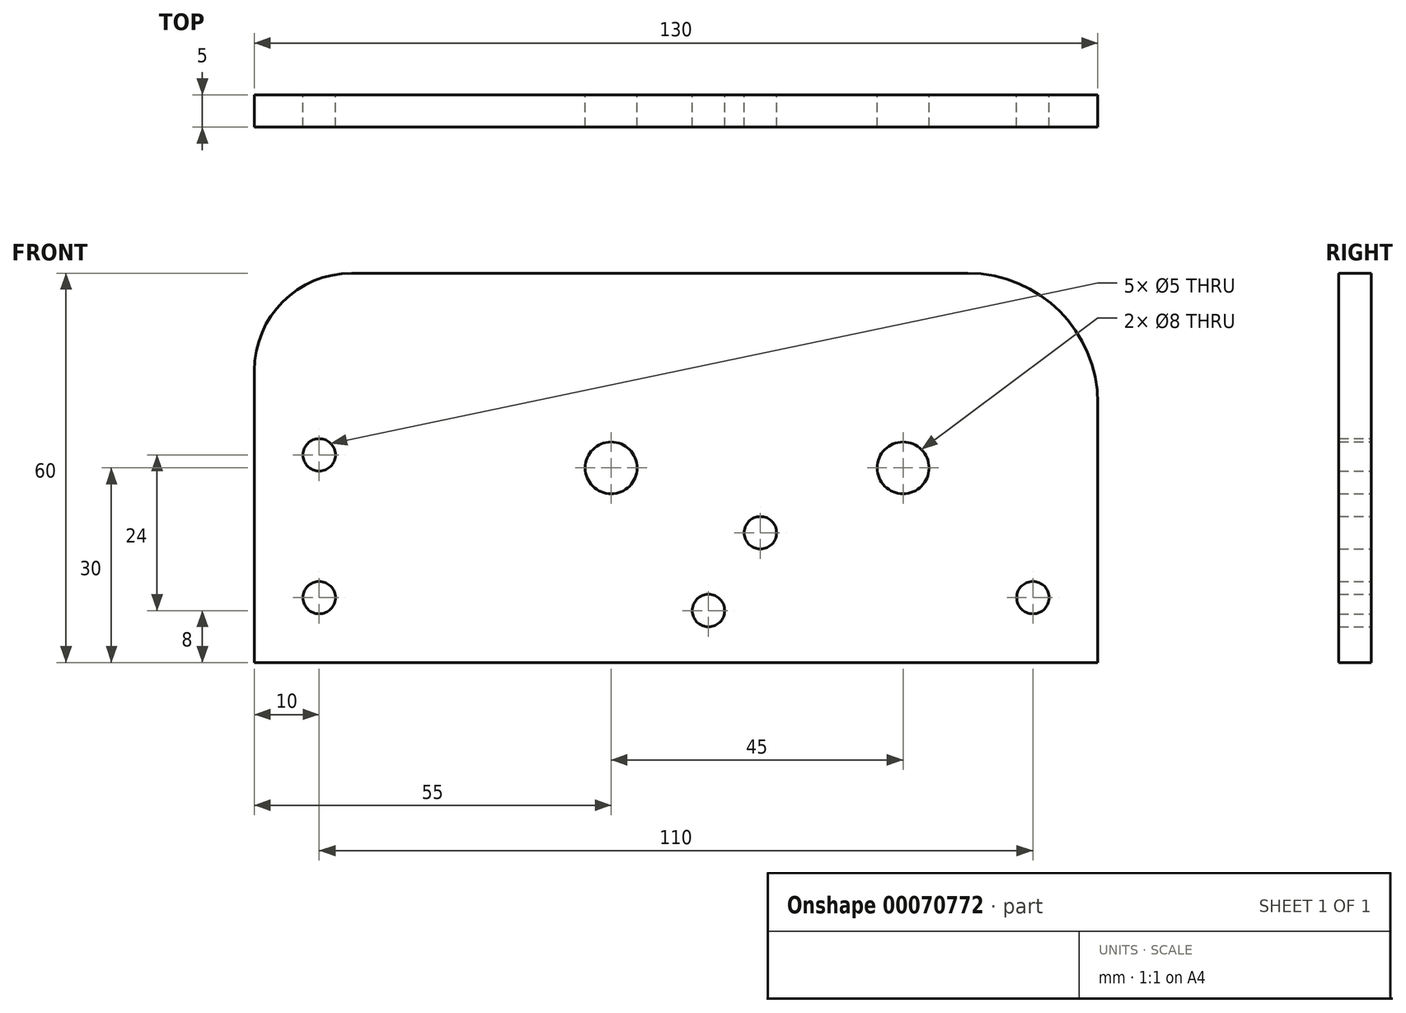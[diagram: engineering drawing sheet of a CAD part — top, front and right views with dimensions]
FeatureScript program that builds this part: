
annotation { "Feature Type Name" : "Feature", "Feature Type Description" : "" }
export const myFeature = defineFeature(function(context is Context, id is Id, definition is map)
    precondition{}
    {
        {
            var Q0;
            Q0=qCreatedBy(makeId("Front.planeOp"),FACE);
            var sketch = newSketch(context, id + "F0", { "sketchPlane" : qUnion([Q0])});
            skLineSegment(sketch, "E0.bottom", {"start": v(0, 0) * mm, "end": v(130, 0) * mm});
            skLineSegment(sketch, "E0.top", {"start": v(15, 60) * mm, "end": v(110, 60) * mm});
            skLineSegment(sketch, "E0.left", {"start": v(0, 0) * mm, "end": v(0, 45) * mm});
            skLineSegment(sketch, "E0.right", {"start": v(130, 0) * mm, "end": v(130, 40) * mm});
            skCircle(sketch, "E1", {"center": v(100, 30) * mm, "radius": 4 * mm});
            skCircle(sketch, "E2", {"center": v(55, 30) * mm, "radius": 4 * mm});
            skCircle(sketch, "E3", {"center": v(10, 10) * mm, "radius": 2.5 * mm});
            skCircle(sketch, "E4", {"center": v(10, 32) * mm, "radius": 2.5 * mm});
            skCircle(sketch, "E5", {"center": v(120, 10) * mm, "radius": 2.5 * mm});
            skCircle(sketch, "E6", {"center": v(70, 8) * mm, "radius": 2.5 * mm});
            skCircle(sketch, "E7", {"center": v(78, 20) * mm, "radius": 2.5 * mm});
            skPoint(sketch, "E8.visualSharp", {"position": v(130, 60) * mm});
            skArc(sketch, "E8.filletArc", {"start": v(130, 40) * mm, "mid": v(124.14, 54.14) * mm, "end": v(110, 60) * mm});
            skPoint(sketch, "E9.visualSharp", {"position": v(0, 60) * mm});
            skArc(sketch, "E9.filletArc", {"start": v(15, 60) * mm, "mid": v(4.4, 55.6) * mm, "end": v(0, 45) * mm});
            skSolve(sketch);
        }
        {
            var Q0;
            Q0=qSketchRegion(id+"F0",true);
            extrude(context, id + "F1", {"entities" : qUnion([Q0]), "depth" : 5 * mm});
        }
    });
